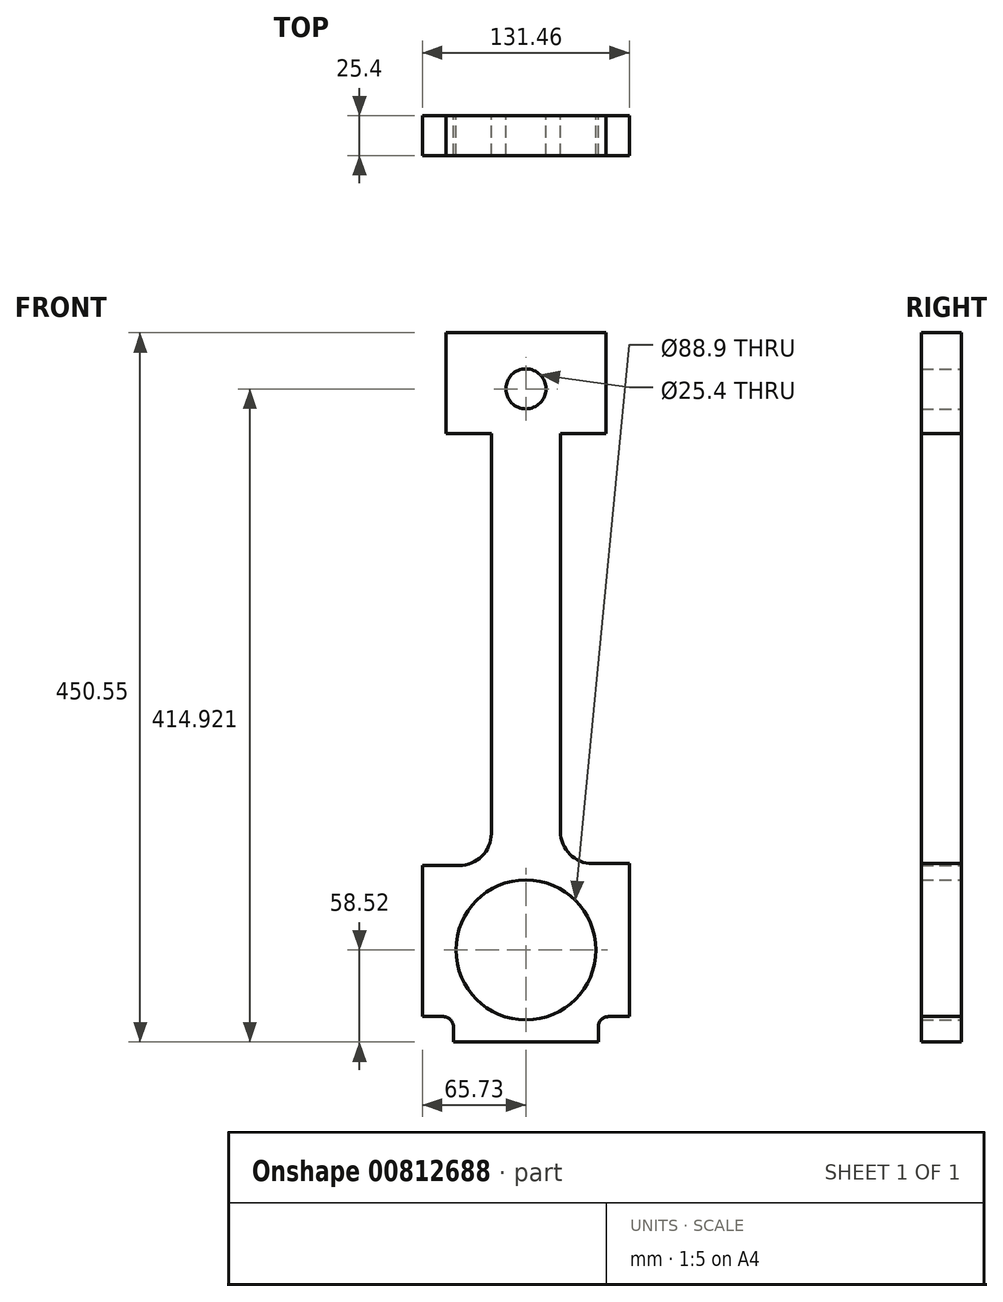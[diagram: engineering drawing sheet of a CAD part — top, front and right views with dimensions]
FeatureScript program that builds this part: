
annotation { "Feature Type Name" : "Feature", "Feature Type Description" : "" }
export const myFeature = defineFeature(function(context is Context, id is Id, definition is map)
    precondition{}
    {
        {
            var Q0;
            Q0=qCreatedBy(makeId("Front.planeOp"),FACE);
            var sketch = newSketch(context, id + "F0", { "sketchPlane" : qUnion([Q0])});
            skCircle(sketch, "E0", {"center": v(0, 0) * mm, "radius": 44.45 * mm});
            skLineSegment(sketch, "E1.bottom", {"start": v(-46.08, -58.52) * mm, "end": v(46.08, -58.52) * mm});
            skLineSegment(sketch, "E1.left", {"start": v(-65.73, -42.35) * mm, "end": v(-65.73, 53.6) * mm});
            skLineSegment(sketch, "E1.right", {"start": v(65.73, -42.35) * mm, "end": v(65.73, 54.82) * mm});
            skLineSegment(sketch, "E2", {"start": v(0, 30.65) * mm, "end": v(0, -29) * mm, "construction": true});
            skLineSegment(sketch, "E3", {"start": v(46.08, -58.52) * mm, "end": v(46.08, -48.7) * mm});
            skLineSegment(sketch, "E4", {"start": v(52.43, -42.35) * mm, "end": v(65.73, -42.35) * mm});
            skLineSegment(sketch, "E5", {"start": v(-46.08, -58.52) * mm, "end": v(-46.08, -48.7) * mm});
            skLineSegment(sketch, "E6", {"start": v(-52.43, -42.35) * mm, "end": v(-65.73, -42.35) * mm});
            skPoint(sketch, "E7.visualSharp", {"position": v(-46.08, -42.35) * mm});
            skArc(sketch, "E7.filletArc", {"start": v(-46.08, -48.7) * mm, "mid": v(-47.94, -44.21) * mm, "end": v(-52.43, -42.35) * mm});
            skPoint(sketch, "E8.visualSharp", {"position": v(46.08, -42.35) * mm});
            skArc(sketch, "E8.filletArc", {"start": v(52.43, -42.35) * mm, "mid": v(47.94, -44.21) * mm, "end": v(46.08, -48.7) * mm});
            skLineSegment(sketch, "E9", {"start": v(-65.73, 53.6) * mm, "end": v(-42.32, 53.6) * mm});
            skLineSegment(sketch, "E10", {"start": v(-22, 73.92) * mm, "end": v(-22, 327.92) * mm});
            skLineSegment(sketch, "E11", {"start": v(65.73, 54.82) * mm, "end": v(42.32, 54.82) * mm});
            skLineSegment(sketch, "E12", {"start": v(22, 75.14) * mm, "end": v(22, 327.92) * mm});
            skPoint(sketch, "E13.visualSharp", {"position": v(-22, 53.6) * mm});
            skArc(sketch, "E13.filletArc", {"start": v(-42.32, 53.6) * mm, "mid": v(-27.95, 59.55) * mm, "end": v(-22, 73.92) * mm});
            skPoint(sketch, "E14.visualSharp", {"position": v(22, 54.82) * mm});
            skArc(sketch, "E14.filletArc", {"start": v(22, 75.14) * mm, "mid": v(27.95, 60.77) * mm, "end": v(42.32, 54.82) * mm});
            skLineSegment(sketch, "E15.bottom", {"start": v(-50.8, 327.92) * mm, "end": v(-16.58, 327.92) * mm});
            skLineSegment(sketch, "E15.top", {"start": v(-50.8, 392.03) * mm, "end": v(50.8, 392.03) * mm});
            skLineSegment(sketch, "E15.left", {"start": v(-50.8, 327.92) * mm, "end": v(-50.8, 392.03) * mm});
            skLineSegment(sketch, "E15.right", {"start": v(50.8, 327.92) * mm, "end": v(50.8, 392.03) * mm});
            skLineSegment(sketch, "E16.left", {"start": v(-16.58, 327.92) * mm, "end": v(-16.58, 327.92) * mm});
            skLineSegment(sketch, "E16.right", {"start": v(-22, 327.92) * mm, "end": v(-22, 321.45) * mm});
            skPoint(sketch, "E17.top.end.orphan", {"position": v(22, 374.95) * mm});
            skPoint(sketch, "E18.orphan", {"position": v(22, 321.78) * mm});
            skLineSegment(sketch, "E19.trimOffspring", {"start": v(22, 327.92) * mm, "end": v(50.8, 327.92) * mm});
            skLineSegment(sketch, "E20", {"start": v(-22, 327.92) * mm, "end": v(-16.58, 327.92) * mm});
            skCircle(sketch, "E21", {"center": v(0, 356.4) * mm, "radius": 12.7 * mm});
            skSolve(sketch);
        }
        {
            var Q0;
            Q0=makeQuery(id+"F0.imprint","IMPRINT",FACE,{"disambiguationData":[TD([[makeQuery(id+"F0.imprint","IMPRINT",EDGE,{"derivedFrom":sQuery(id+"F0.wireOp",EDGE,"E0")}),-1.0]])]});
            extrude(context, id + "F1", {"entities" : qUnion([Q0]), "depth" : 25.4 * mm, "offsetDistance" : 25.4 * mm});
        }
    });
